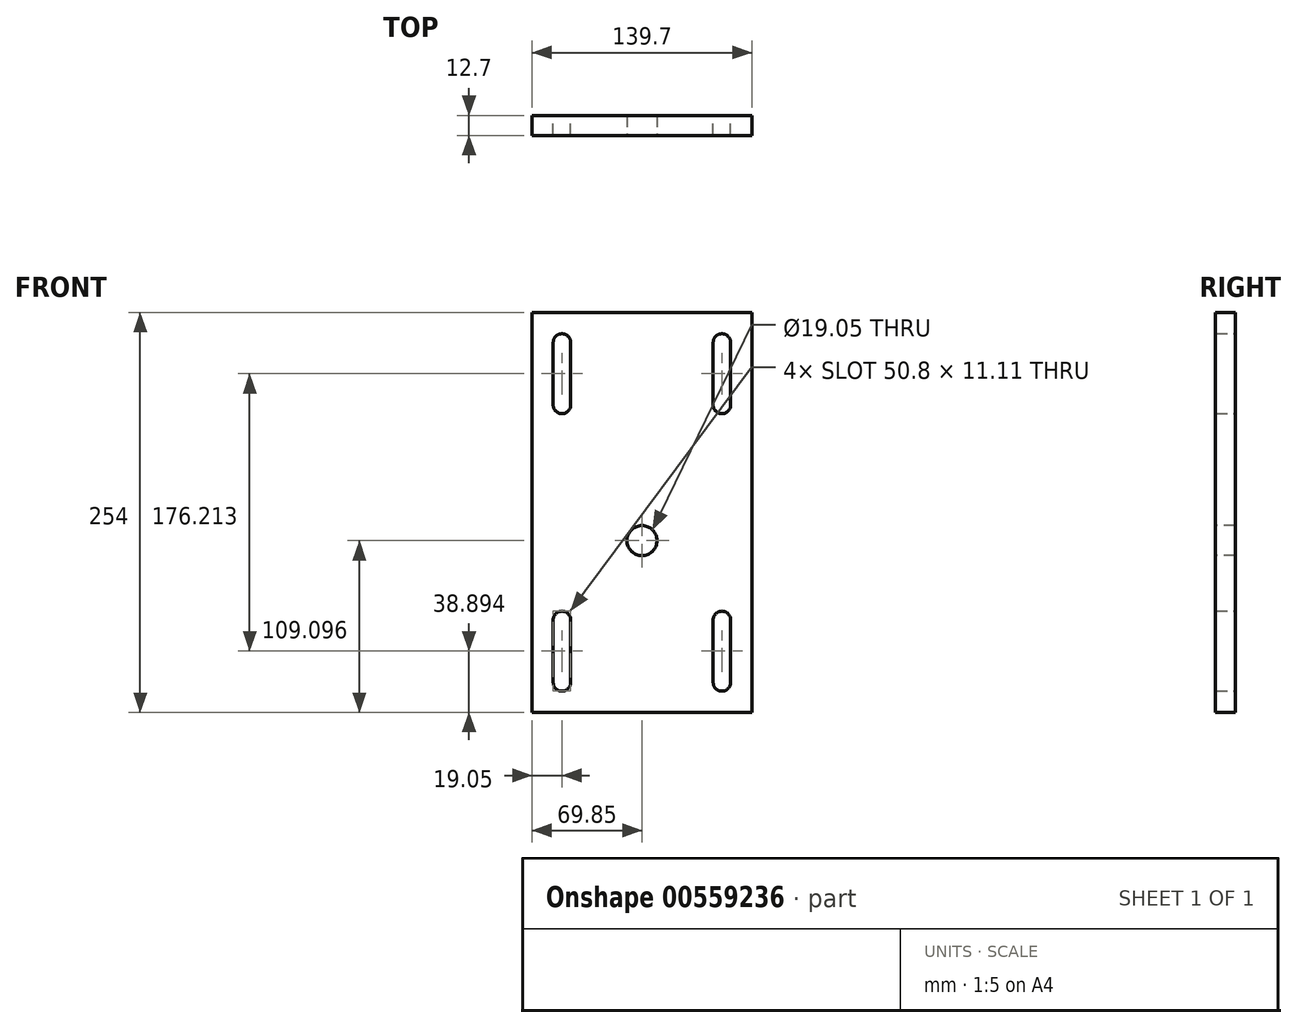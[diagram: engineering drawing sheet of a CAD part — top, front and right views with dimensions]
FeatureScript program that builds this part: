
annotation { "Feature Type Name" : "Feature", "Feature Type Description" : "" }
export const myFeature = defineFeature(function(context is Context, id is Id, definition is map)
    precondition{}
    {
        {
            var Q0;
            Q0=qCreatedBy(makeId("Front.planeOp"),FACE);
            var sketch = newSketch(context, id + "F0", { "sketchPlane" : qUnion([Q0])});
            skLineSegment(sketch, "E0.bottom", {"start": v(69.85, -127) * mm, "end": v(-69.85, -127) * mm});
            skLineSegment(sketch, "E0.top", {"start": v(69.85, 127) * mm, "end": v(-69.85, 127) * mm});
            skLineSegment(sketch, "E0.left", {"start": v(69.85, -127) * mm, "end": v(69.85, 127) * mm});
            skLineSegment(sketch, "E0.right", {"start": v(-69.85, -127) * mm, "end": v(-69.85, 127) * mm});
            skPoint(sketch, "E0.middle", {"position": v(0, 0) * mm});
            skArc(sketch, "E1", {"start": v(-45.24, 107.95) * mm, "mid": v(-50.82, 113.5) * mm, "end": v(-56.36, 107.92) * mm});
            skArc(sketch, "E2", {"start": v(-56.36, 68.26) * mm, "mid": v(-50.8, 62.7) * mm, "end": v(-45.24, 68.26) * mm});
            skLineSegment(sketch, "E3", {"start": v(-56.36, 107.98) * mm, "end": v(-56.36, 68.26) * mm});
            skLineSegment(sketch, "E4", {"start": v(-45.24, 68.26) * mm, "end": v(-45.24, 107.95) * mm});
            skArc(sketch, "E5.MirrorCS", {"start": v(45.24, 107.95) * mm, "mid": v(50.82, 113.5) * mm, "end": v(56.36, 107.92) * mm});
            skArc(sketch, "E6.MirrorCS", {"start": v(56.36, 68.26) * mm, "mid": v(50.8, 62.7) * mm, "end": v(45.24, 68.26) * mm});
            skLineSegment(sketch, "E7.MirrorCS", {"start": v(56.36, 107.98) * mm, "end": v(56.36, 68.26) * mm});
            skLineSegment(sketch, "E8.MirrorCS", {"start": v(45.24, 68.26) * mm, "end": v(45.24, 107.95) * mm});
            skArc(sketch, "E9.MirrorCS", {"start": v(56.36, -68.26) * mm, "mid": v(50.8, -62.7) * mm, "end": v(45.24, -68.26) * mm});
            skArc(sketch, "E10.MirrorCS", {"start": v(-56.36, -68.26) * mm, "mid": v(-50.8, -62.7) * mm, "end": v(-45.24, -68.26) * mm});
            skLineSegment(sketch, "E11.MirrorCS", {"start": v(45.24, -68.26) * mm, "end": v(45.24, -107.95) * mm});
            skLineSegment(sketch, "E12.MirrorCS", {"start": v(56.36, -107.98) * mm, "end": v(56.36, -68.26) * mm});
            skArc(sketch, "E13.MirrorCS", {"start": v(45.24, -107.95) * mm, "mid": v(50.82, -113.5) * mm, "end": v(56.36, -107.92) * mm});
            skLineSegment(sketch, "E14.MirrorCS", {"start": v(-45.24, -68.26) * mm, "end": v(-45.24, -107.95) * mm});
            skLineSegment(sketch, "E15.MirrorCS", {"start": v(-56.36, -107.98) * mm, "end": v(-56.36, -68.26) * mm});
            skArc(sketch, "E16.MirrorCS", {"start": v(-45.24, -107.95) * mm, "mid": v(-50.82, -113.5) * mm, "end": v(-56.36, -107.92) * mm});
            skSolve(sketch);
        }
        {
            var Q0;
            Q0 = qSketchRegion(id + "F0", true);
            extrude(context, id + "F1", {"entities" : qUnion([Q0]), "depth" : 12.7 * mm, "offsetDistance" : 25.4 * mm});
        }
        {
            var Q0;
            Q0=makeQuery(id+"F1.opExtrude","CAP_FACE",FACE,{"disambiguationData":[OSD([sQuery(id+"F0.wireOp",EDGE,"E0.bottom"),sQuery(id+"F0.wireOp",EDGE,"E0.top"),sQuery(id+"F0.wireOp",EDGE,"E0.left"),sQuery(id+"F0.wireOp",EDGE,"E0.right"),sQuery(id+"F0.wireOp",EDGE,"E1"),sQuery(id+"F0.wireOp",EDGE,"E2"),sQuery(id+"F0.wireOp",EDGE,"E3"),sQuery(id+"F0.wireOp",EDGE,"E4"),sQuery(id+"F0.wireOp",EDGE,"E5.MirrorCS"),sQuery(id+"F0.wireOp",EDGE,"E6.MirrorCS"),sQuery(id+"F0.wireOp",EDGE,"E7.MirrorCS"),sQuery(id+"F0.wireOp",EDGE,"E8.MirrorCS"),sQuery(id+"F0.wireOp",EDGE,"E9.MirrorCS"),sQuery(id+"F0.wireOp",EDGE,"E10.MirrorCS"),sQuery(id+"F0.wireOp",EDGE,"E11.MirrorCS"),sQuery(id+"F0.wireOp",EDGE,"E12.MirrorCS"),sQuery(id+"F0.wireOp",EDGE,"E13.MirrorCS"),sQuery(id+"F0.wireOp",EDGE,"E14.MirrorCS"),sQuery(id+"F0.wireOp",EDGE,"E15.MirrorCS"),sQuery(id+"F0.wireOp",EDGE,"E16.MirrorCS")])],"isStart":false});
            var sketch = newSketch(context, id + "F2", { "sketchPlane" : qUnion([Q0])});
            skCircle(sketch, "E17", {"center": v(0, -17.9) * mm, "radius": 9.53 * mm});
            skSolve(sketch);
        }
        {
            var Q0;
            Q0=makeQuery(id+"F2.imprint","IMPRINT",FACE,{"disambiguationData":[TD([[makeQuery(id+"F2.imprint","IMPRINT",EDGE,{"derivedFrom":sQuery(id+"F2.wireOp",EDGE,"E17")}),1.0]])]});
            extrude(context, id + "F3", {"entities" : qUnion([Q0]), "operationType" : NewBodyOperationType.REMOVE, "oppositeDirection" : true, "depth" : 25.4 * mm, "offsetDistance" : 25.4 * mm});
        }
    });
